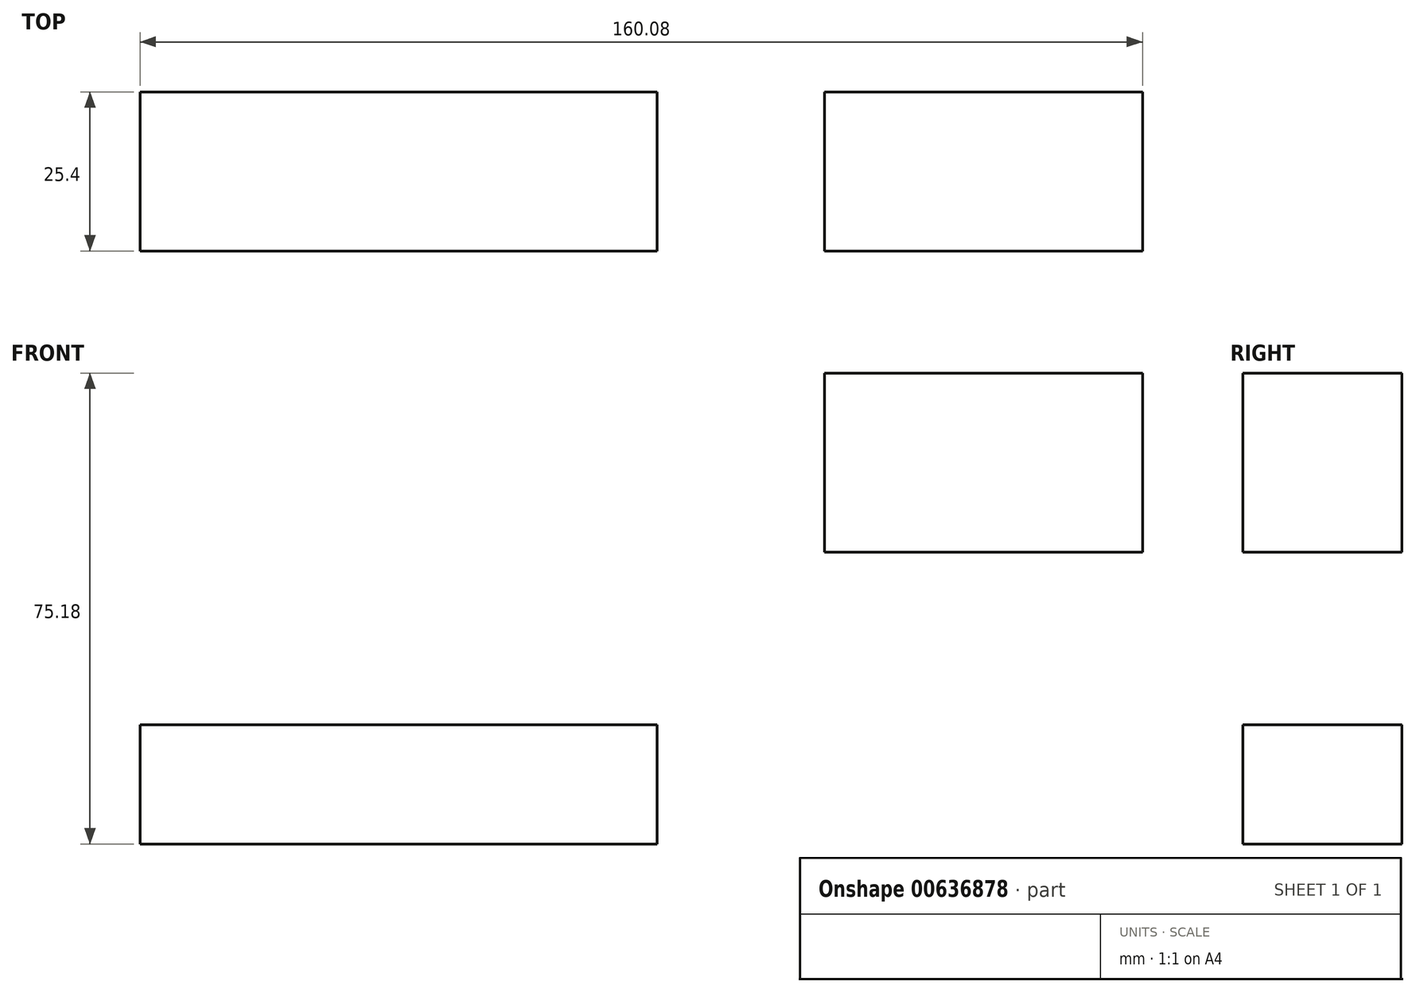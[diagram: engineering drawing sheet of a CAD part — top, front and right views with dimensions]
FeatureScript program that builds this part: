
annotation { "Feature Type Name" : "Feature", "Feature Type Description" : "" }
export const myFeature = defineFeature(function(context is Context, id is Id, definition is map)
    precondition{}
    {
        {
            var Q0;
            Q0=qCreatedBy(makeId("Front.planeOp"),FACE);
            var sketch = newSketch(context, id + "F0", { "sketchPlane" : qUnion([Q0])});
            skLineSegment(sketch, "E0.bottom", {"start": v(-41.28, 9.52) * mm, "end": v(41.27, 9.53) * mm});
            skLineSegment(sketch, "E0.top", {"start": v(-41.28, -9.53) * mm, "end": v(41.28, -9.53) * mm});
            skLineSegment(sketch, "E0.left", {"start": v(-41.28, 9.52) * mm, "end": v(-41.28, -9.53) * mm});
            skLineSegment(sketch, "E0.right", {"start": v(41.27, 9.53) * mm, "end": v(41.28, -9.52) * mm});
            skPoint(sketch, "E0.middle", {"position": v(0, 0) * mm});
            skLineSegment(sketch, "E1.bottom", {"start": v(68.01, 37.08) * mm, "end": v(118.81, 37.08) * mm});
            skLineSegment(sketch, "E1.top", {"start": v(68.01, 65.65) * mm, "end": v(118.81, 65.65) * mm});
            skLineSegment(sketch, "E1.left", {"start": v(68.01, 37.08) * mm, "end": v(68.01, 65.65) * mm});
            skLineSegment(sketch, "E1.right", {"start": v(118.81, 37.08) * mm, "end": v(118.81, 65.65) * mm});
            skPoint(sketch, "E1.middle", {"position": v(93.41, 51.37) * mm});
            skLineSegment(sketch, "E2", {"start": v(41.27, 9.53) * mm, "end": v(41.27, 41.66) * mm});
            skArc(sketch, "E3", {"start": v(41.27, 41.66) * mm, "mid": v(46.99, 53.85) * mm, "end": v(60.02, 57.27) * mm});
            skLineSegment(sketch, "E4", {"start": v(60.02, 57.27) * mm, "end": v(93.03, 57.27) * mm});
            skSolve(sketch);
        }
        {
            var Q0;
            Q0=qSketchRegion(id+"F0",true);
            extrude(context, id + "F1", {"entities" : qUnion([Q0]), "depth" : 25.4 * mm, "offsetDistance" : 25.4 * mm});
        }
    });
